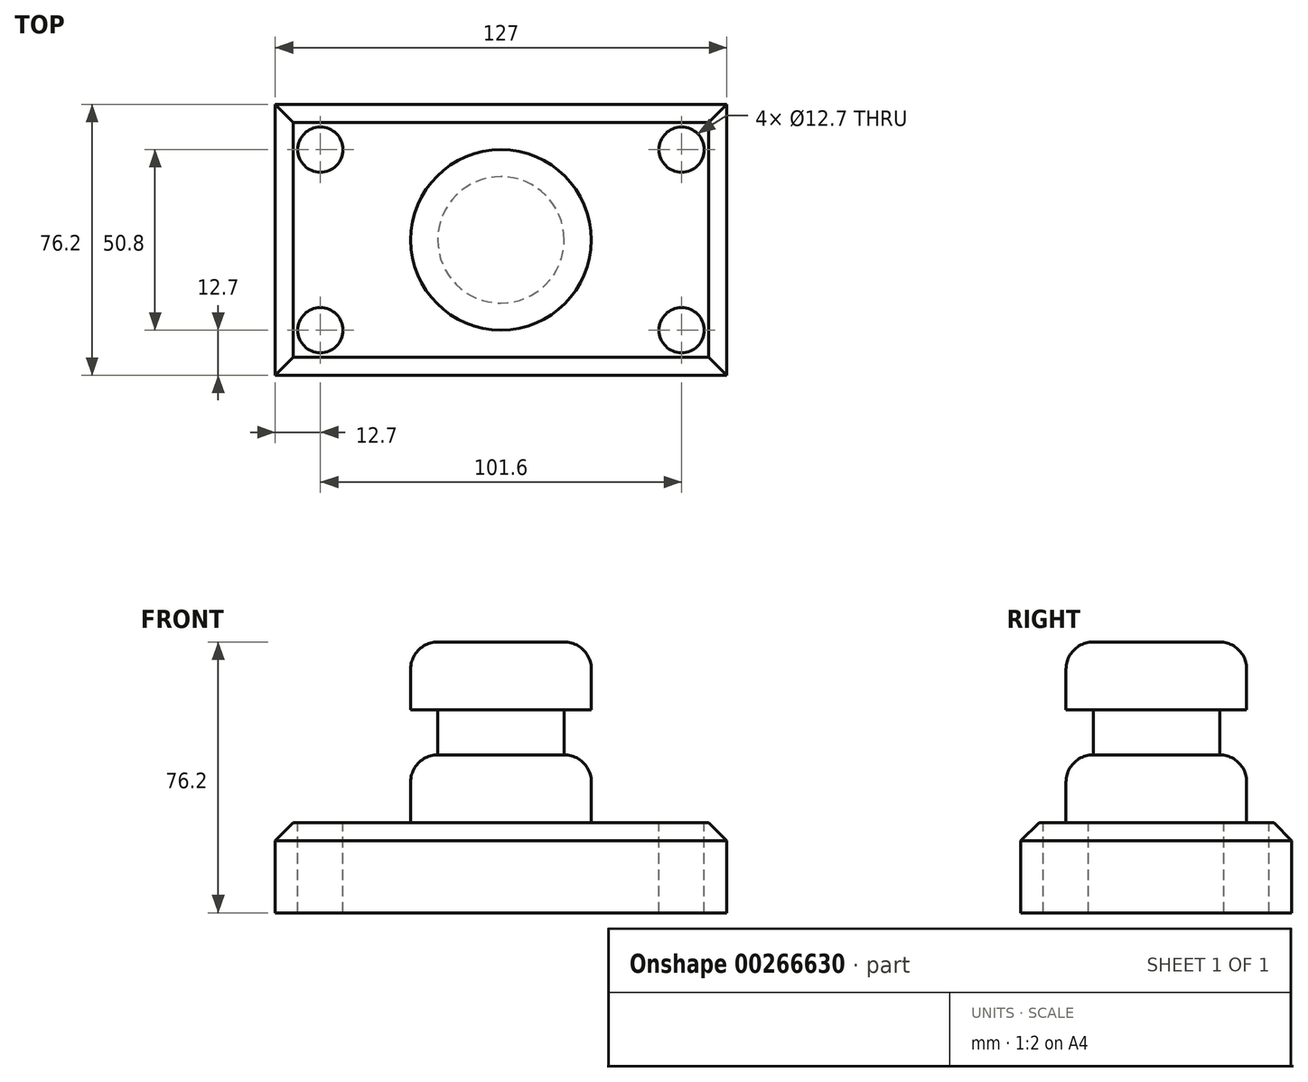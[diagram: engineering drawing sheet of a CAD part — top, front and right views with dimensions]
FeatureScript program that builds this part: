
annotation { "Feature Type Name" : "Feature", "Feature Type Description" : "" }
export const myFeature = defineFeature(function(context is Context, id is Id, definition is map)
    precondition{}
    {
        {
            var Q0;
            Q0=qCreatedBy(makeId("Top.planeOp"),FACE);
            var sketch = newSketch(context, id + "F0", { "sketchPlane" : qUnion([Q0])});
            skLineSegment(sketch, "E0.bottom", {"start": v(-63.5, 38.1) * mm, "end": v(63.5, 38.1) * mm});
            skLineSegment(sketch, "E0.top", {"start": v(-63.5, -38.1) * mm, "end": v(63.5, -38.1) * mm});
            skLineSegment(sketch, "E0.left", {"start": v(-63.5, 38.1) * mm, "end": v(-63.5, -38.1) * mm});
            skLineSegment(sketch, "E0.right", {"start": v(63.5, 38.1) * mm, "end": v(63.5, -38.1) * mm});
            skPoint(sketch, "E0.middle", {"position": v(0, 0) * mm});
            skSolve(sketch);
        }
        {
            var Q0;
            Q0=makeQuery(id+"F0.imprint","IMPRINT",FACE,{"disambiguationData":[TD([[makeQuery(id+"F0.imprint","IMPRINT",EDGE,{"derivedFrom":sQuery(id+"F0.wireOp",EDGE,"E0.bottom")}),-1.0]])]});
            extrude(context, id + "F1", {"entities" : qUnion([Q0]), "endBound" : BoundingType.SYMMETRIC, "depth" : 25.4 * mm});
        }
        {
            var Q0;
            Q0=makeQuery(id+"F1.opExtrude","CAP_FACE",FACE,{"disambiguationData":[OSD([sQuery(id+"F0.wireOp",EDGE,"E0.bottom"),sQuery(id+"F0.wireOp",EDGE,"E0.top"),sQuery(id+"F0.wireOp",EDGE,"E0.left"),sQuery(id+"F0.wireOp",EDGE,"E0.right")])],"isStart":false});
            var sketch = newSketch(context, id + "F2", { "sketchPlane" : qUnion([Q0])});
            skCircle(sketch, "E1", {"center": v(-50.8, 25.4) * mm, "radius": 6.35 * mm});
            skCircle(sketch, "E2", {"center": v(50.8, 25.4) * mm, "radius": 6.35 * mm});
            skCircle(sketch, "E3", {"center": v(50.8, -25.4) * mm, "radius": 6.35 * mm});
            skCircle(sketch, "E4", {"center": v(-50.8, -25.4) * mm, "radius": 6.35 * mm});
            skSolve(sketch);
        }
        {
            var Q0;
            Q0 = qSketchRegion(id + "F2", true);
            extrude(context, id + "F3", {"entities" : qUnion([Q0]), "operationType" : NewBodyOperationType.REMOVE, "oppositeDirection" : true, "depth" : 38.1 * mm});
        }
        {
            var Q0;
            Q0=qCreatedBy(makeId("Front.planeOp"),FACE);
            var sketch = newSketch(context, id + "F4", { "sketchPlane" : qUnion([Q0])});
            skLineSegment(sketch, "E5.bottom", {"start": v(0, 12.7) * mm, "end": v(-25.4, 12.7) * mm});
            skLineSegment(sketch, "E5.top", {"start": v(0, 63.5) * mm, "end": v(-25.4, 63.5) * mm});
            skLineSegment(sketch, "E5.left", {"start": v(0, 12.7) * mm, "end": v(0, 63.5) * mm});
            skLineSegment(sketch, "E5.right", {"start": v(-25.4, 12.7) * mm, "end": v(-25.4, 63.5) * mm});
            skSolve(sketch);
        }
        {
            var Q0;
            Q0=makeQuery(id+"F4.imprint","IMPRINT",FACE,{"disambiguationData":[TD([[makeQuery(id+"F4.imprint","IMPRINT",EDGE,{"derivedFrom":sQuery(id+"F4.wireOp",EDGE,"E5.bottom")}),-1.0]])]});
            var Q1;
            Q1=sQuery(id+"F4.wireOp",EDGE,"E5.left");
            revolve(context, id + "F5", {"operationType" : NewBodyOperationType.ADD, "entities" : qUnion([Q0]), "axis" : qUnion([Q1]), "revolveType" : RevolveType.FULL, "oppositeDirection" : true});
        }
        {
            var Q0;
            Q0=qCreatedBy(makeId("Front.planeOp"),FACE);
            var sketch = newSketch(context, id + "F6", { "sketchPlane" : qUnion([Q0])});
            skLineSegment(sketch, "E6.bottom", {"start": v(-17.78, 31.75) * mm, "end": v(-33.82, 31.75) * mm});
            skLineSegment(sketch, "E6.top", {"start": v(-17.78, 44.45) * mm, "end": v(-33.82, 44.45) * mm});
            skLineSegment(sketch, "E6.left", {"start": v(-17.78, 31.75) * mm, "end": v(-17.78, 44.45) * mm});
            skLineSegment(sketch, "E6.right", {"start": v(-33.82, 31.75) * mm, "end": v(-33.82, 44.45) * mm});
            skSolve(sketch);
        }
        {
            var Q0;
            Q0=makeQuery(id+"F6.imprint","IMPRINT",FACE,{"disambiguationData":[TD([[makeQuery(id+"F6.imprint","IMPRINT",EDGE,{"derivedFrom":sQuery(id+"F6.wireOp",EDGE,"E6.bottom")}),-1.0]])]});
            var Q1;
            Q1=makeQuery(id+"F5.opRevolve","SWEPT_FACE",FACE,{"disambiguationData":[OSD([sQuery(id+"F4.wireOp",EDGE,"E5.right")])]});
            revolve(context, id + "F7", {"operationType" : NewBodyOperationType.REMOVE, "entities" : qUnion([Q0]), "axis" : qUnion([Q1]), "revolveType" : RevolveType.FULL, "oppositeDirection" : true});
        }
        {
            var Q0;
            Q0=makeQuery(id+"F1.opExtrude","CAP_EDGE",EDGE,{"disambiguationData":[OSD([sQuery(id+"F0.wireOp",EDGE,"E0.top")])],"isStart":false});
            var Q1;
            Q1=makeQuery(id+"F1.opExtrude","CAP_EDGE",EDGE,{"disambiguationData":[OSD([sQuery(id+"F0.wireOp",EDGE,"E0.left")])],"isStart":false});
            var Q2;
            Q2=makeQuery(id+"F1.opExtrude","CAP_EDGE",EDGE,{"disambiguationData":[OSD([sQuery(id+"F0.wireOp",EDGE,"E0.bottom")])],"isStart":false});
            var Q3;
            Q3=makeQuery(id+"F1.opExtrude","CAP_EDGE",EDGE,{"disambiguationData":[OSD([sQuery(id+"F0.wireOp",EDGE,"E0.right")])],"isStart":false});
            chamfer(context, id + "F8", {"entities" : qUnion([Q0, Q1, Q2, Q3]), "width" : 5.08 * mm, "tangentPropagation" : true});
        }
        {
            var Q0;
            Q0=makeQuery(id+"F5.opRevolve","SWEPT_EDGE",EDGE,{"disambiguationData":[OSD([sQuery(id+"F4.wireOp",EDGE,"E5.bottom"),sQuery(id+"F4.wireOp",EDGE,"E5.right")])]});
            var Q1;
            Q1=makeQuery(id+"F7.boolean.opBoolean","INTERSECT",EDGE,{"derivedFrom":[makeQuery(id+"F5.opRevolve","SWEPT_FACE",FACE,{"disambiguationData":[OSD([sQuery(id+"F4.wireOp",EDGE,"E5.right")])]}),makeQuery(id+"F7.opRevolve","SWEPT_FACE",FACE,{"disambiguationData":[OSD([sQuery(id+"F6.wireOp",EDGE,"E6.bottom")])]})]});
            var Q2;
            Q2=makeQuery(id+"F5.opRevolve","SWEPT_EDGE",EDGE,{"disambiguationData":[OSD([sQuery(id+"F4.wireOp",EDGE,"E5.top"),sQuery(id+"F4.wireOp",EDGE,"E5.right")])]});
            fillet(context, id + "F9", {"entities" : qUnion([Q0, Q1, Q2]), "radius" : 7.62 * mm, "tangentPropagation" : true, "allowEdgeOverflow" : false});
        }
    });
